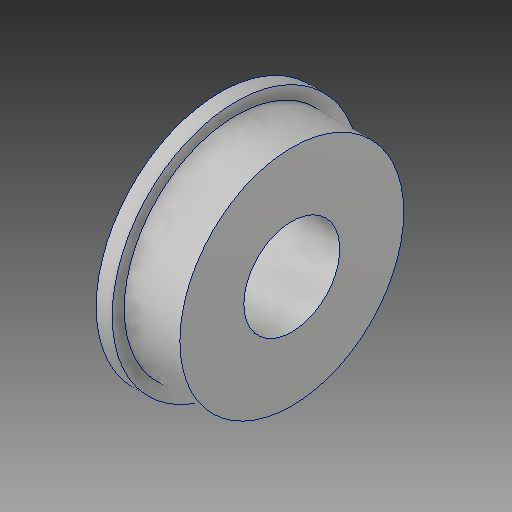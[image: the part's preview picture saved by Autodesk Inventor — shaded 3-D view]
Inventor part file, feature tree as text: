
AUTODESK INVENTOR PART (.ipt)
format: ipt  version: 2017 (Build 210142000, 142)  size: 128,000 bytes
history: native  units: in
note: dims shown in document units (in); Inventor stores cm internally (conversion verified against a paired STEP export)
features: revolve x1
ambient origin geometry x8: Origin, YZ Plane, XZ Plane, XY Plane, X Axis, Y Axis, Z Axis, Center Point
bodies: Solid1 (feature_tree)
feature tree (1):
  revolve  "Revolve1"  [1 undecoded]
note: 1 required parameter value undecoded (feature->parameter linkage not recoverable at this tier; creation-order binding heuristic only, values carry confidence <= 0.55)
